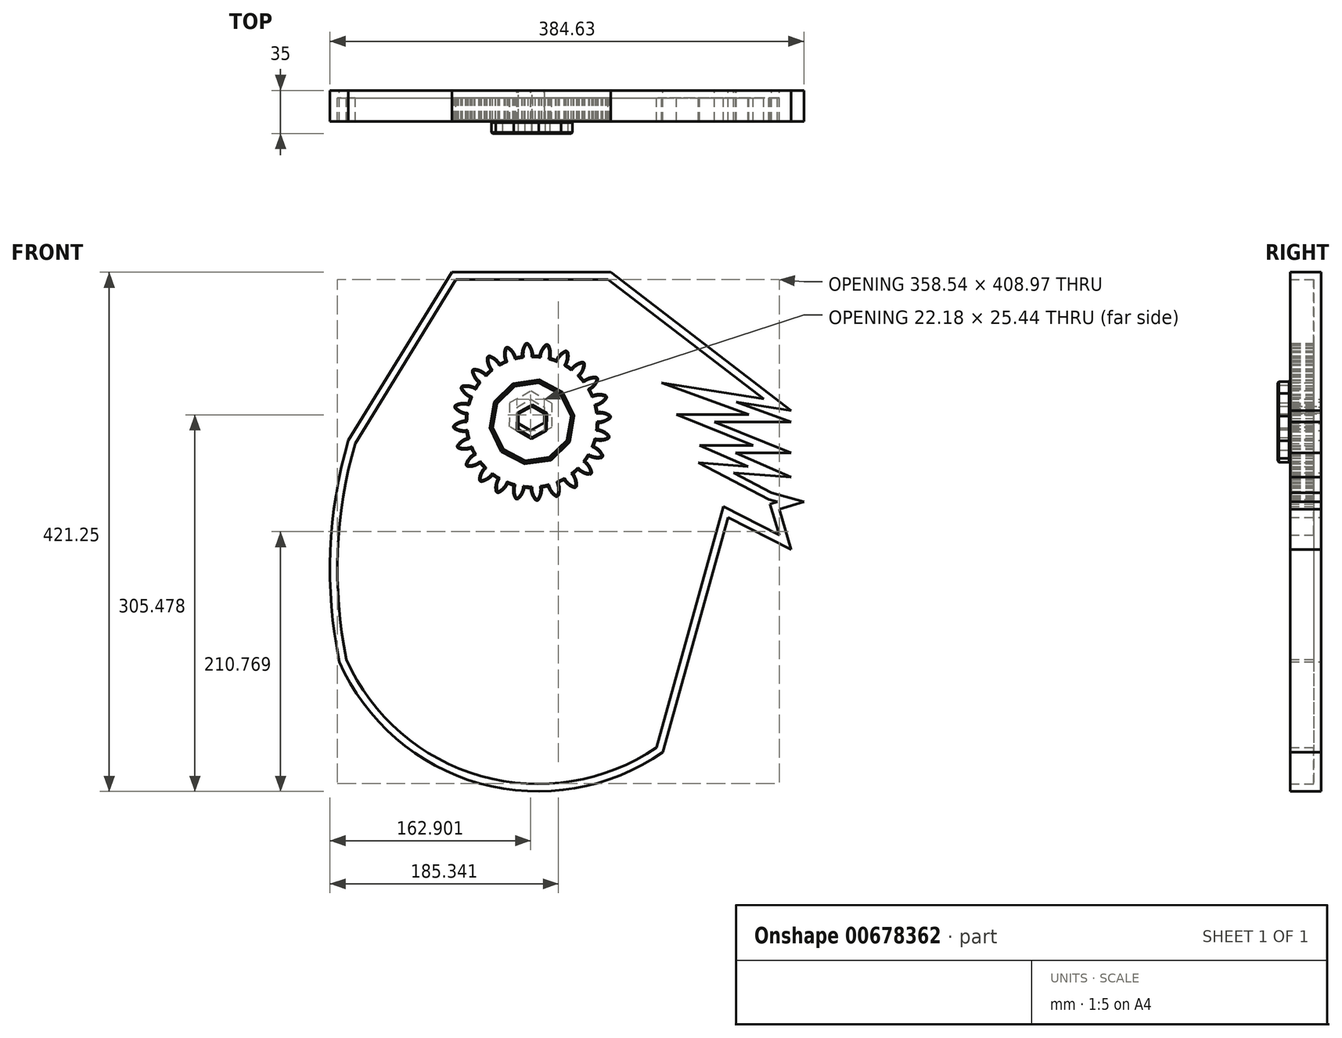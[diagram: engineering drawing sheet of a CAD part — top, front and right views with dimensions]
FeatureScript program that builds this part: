
annotation { "Feature Type Name" : "Feature", "Feature Type Description" : "" }
export const myFeature = defineFeature(function(context is Context, id is Id, definition is map)
    precondition{}
    {
        {
            var Q0;
            Q0=qCreatedBy(makeId("Front.planeOp"),FACE);
            var sketch = newSketch(context, id + "F0", { "sketchPlane" : qUnion([Q0])});
            skCircle(sketch, "E0", {"center": v(0, 0) * mm, "radius": 53.72 * mm});
            skCircle(sketch, "E1", {"center": v(0, 0) * mm, "radius": 58.67 * mm, "construction": true});
            skCircle(sketch, "E2", {"center": v(0, 0) * mm, "radius": 63.5 * mm, "construction": true});
            skLineSegment(sketch, "E3", {"start": v(0, 0) * mm, "end": v(0, 78.03) * mm, "construction": true});
            skLineSegment(sketch, "E4", {"start": v(0, 0) * mm, "end": v(-5.6, 85.42) * mm, "construction": true});
            skLineSegment(sketch, "E5", {"start": v(0, 58.67) * mm, "end": v(-59.1, 58.67) * mm, "construction": true});
            skLineSegment(sketch, "E6", {"start": v(0, 58.67) * mm, "end": v(-58.88, 37.24) * mm, "construction": true});
            skCircle(sketch, "E7", {"center": v(0, 0) * mm, "radius": 55.14 * mm, "construction": true});
            skCircle(sketch, "E8", {"center": v(0, 58.67) * mm, "radius": 14.6 * mm, "construction": true});
            skCircle(sketch, "E9", {"center": v(-13.72, 53.68) * mm, "radius": 14.6 * mm, "construction": true});
            skArc(sketch, "E10", {"start": v(0, 58.67) * mm, "mid": v(-1.2, 61.2) * mm, "end": v(-2.86, 63.44) * mm});
            skArc(sketch, "E11", {"start": v(0.88, 53.71) * mm, "mid": v(0.65, 56.23) * mm, "end": v(0, 58.67) * mm});
            skArc(sketch, "E12.MirrorCS", {"start": v(-7.66, 58.17) * mm, "mid": v(-6.8, 60.83) * mm, "end": v(-5.45, 63.27) * mm});
            skArc(sketch, "E13.MirrorCS", {"start": v(-7.88, 53.14) * mm, "mid": v(-7.99, 55.67) * mm, "end": v(-7.66, 58.17) * mm});
            skArc(sketch, "E14", {"start": v(-2.86, 63.44) * mm, "mid": v(-4.18, 63.85) * mm, "end": v(-5.45, 63.27) * mm});
            skCircle(sketch, "E15.cCircle", {"center": v(0, 0) * mm, "radius": 31.52 * mm, "construction": true});
            skLineSegment(sketch, "E15.0", {"start": v(-5.65, -32.65) * mm, "end": v(-23.76, -23.1) * mm});
            skLineSegment(sketch, "E15.1", {"start": v(-23.76, -23.1) * mm, "end": v(-32.8, -4.72) * mm});
            skLineSegment(sketch, "E15.2", {"start": v(-32.8, -4.72) * mm, "end": v(-29.31, 15.46) * mm});
            skLineSegment(sketch, "E15.3", {"start": v(-29.31, 15.46) * mm, "end": v(-14.63, 29.74) * mm});
            skLineSegment(sketch, "E15.4", {"start": v(-14.63, 29.74) * mm, "end": v(5.65, 32.65) * mm});
            skLineSegment(sketch, "E15.5", {"start": v(5.65, 32.65) * mm, "end": v(23.76, 23.1) * mm});
            skLineSegment(sketch, "E15.6", {"start": v(23.76, 23.1) * mm, "end": v(32.8, 4.72) * mm});
            skLineSegment(sketch, "E15.7", {"start": v(32.8, 4.72) * mm, "end": v(29.31, -15.46) * mm});
            skLineSegment(sketch, "E15.8", {"start": v(29.31, -15.46) * mm, "end": v(14.63, -29.74) * mm});
            skLineSegment(sketch, "E15.9", {"start": v(14.63, -29.74) * mm, "end": v(-5.65, -32.65) * mm});
            skPoint(sketch, "E15.0.midPoint", {"position": v(-14.7, -27.88) * mm});
            skCircle(sketch, "E16.cCircle", {"center": v(0, 0) * mm, "radius": 11.02 * mm, "construction": true});
            skLineSegment(sketch, "E16.0", {"start": v(-0.15, -12.72) * mm, "end": v(-11.1, -6.23) * mm});
            skLineSegment(sketch, "E16.1", {"start": v(-11.1, -6.23) * mm, "end": v(-10.94, 6.5) * mm});
            skLineSegment(sketch, "E16.2", {"start": v(-10.94, 6.5) * mm, "end": v(0.15, 12.72) * mm});
            skLineSegment(sketch, "E16.3", {"start": v(0.15, 12.72) * mm, "end": v(11.1, 6.23) * mm});
            skLineSegment(sketch, "E16.4", {"start": v(11.1, 6.23) * mm, "end": v(10.94, -6.5) * mm});
            skLineSegment(sketch, "E16.5", {"start": v(10.94, -6.5) * mm, "end": v(-0.15, -12.72) * mm});
            skPoint(sketch, "E16.0.midPoint", {"position": v(-5.62, -9.48) * mm});
            skSolve(sketch);
        }
        {
            var Q0;
            {var subQ0=sQuery(id+"F0.wireOp",EDGE,"E0");var subQ1=makeQuery(id+"F0.imprint","INTERSECT",VERTEX,{"derivedFrom":[subQ0,sQuery(id+"F0.wireOp",EDGE,"E11")]});Q0=makeQuery(id+"F0.imprint","IMPRINT",FACE,{"disambiguationData":[TD([[makeQuery(id+"F0.imprint","IMPRINT",EDGE,{"disambiguationData":[TD([[subQ1,-1.0]])],"derivedFrom":subQ0}),1.0]])]});}
            var Q1;
            Q1=makeQuery(id+"F0.imprint","IMPRINT",FACE,{"disambiguationData":[TD([[makeQuery(id+"F0.imprint","IMPRINT",EDGE,{"derivedFrom":sQuery(id+"F0.wireOp",EDGE,"E10")}),1.0]])]});
            extrude(context, id + "F1", {"entities" : qUnion([Q0, Q1]), "depth" : 25 * mm, "offsetDistance" : 25 * mm});
        }
        {
            var Q0;
            Q0=makeQuery(id+"F1.opExtrude","SWEPT_BODY",BODY,{"disambiguationData":[OSD([sQuery(id+"F0.wireOp",EDGE,"E0"),sQuery(id+"F0.wireOp",EDGE,"E10"),sQuery(id+"F0.wireOp",EDGE,"E11"),sQuery(id+"F0.wireOp",EDGE,"E12.MirrorCS"),sQuery(id+"F0.wireOp",EDGE,"E13.MirrorCS"),sQuery(id+"F0.wireOp",EDGE,"E14")])]});
            var Q1;
            Q1=makeQuery(id+"F1.opExtrude","SWEPT_FACE",FACE,{"disambiguationData":[OSD([sQuery(id+"F0.wireOp",EDGE,"E0")])]});
            circularPattern(context, id + "F2", {"entities" : qUnion([Q0]), "axis" : qUnion([Q1]), "angle" : 360 * degree, "instanceCount" : 24, "equalSpace" : true});
        }
        {
            var Q0;
            Q0=makeQuery(id+"F0.imprint","IMPRINT",FACE,{"disambiguationData":[TD([[makeQuery(id+"F0.imprint","IMPRINT",EDGE,{"derivedFrom":sQuery(id+"F0.wireOp",EDGE,"E15.0")}),-1.0]])]});
            extrude(context, id + "F3", {"entities" : qUnion([Q0]), "operationType" : NewBodyOperationType.ADD, "depth" : 35 * mm, "offsetDistance" : 25 * mm});
        }
        {
            var Q0;
            {var subQ0=makeQuery(id+"F1.opExtrude","CAP_FACE",FACE,{"disambiguationData":[OSD([sQuery(id+"F0.wireOp",EDGE,"E0"),sQuery(id+"F0.wireOp",EDGE,"E10"),sQuery(id+"F0.wireOp",EDGE,"E11"),sQuery(id+"F0.wireOp",EDGE,"E12.MirrorCS"),sQuery(id+"F0.wireOp",EDGE,"E13.MirrorCS"),sQuery(id+"F0.wireOp",EDGE,"E14"),sQuery(id+"F0.wireOp",EDGE,"E15.0"),sQuery(id+"F0.wireOp",EDGE,"E15.1"),sQuery(id+"F0.wireOp",EDGE,"E15.2"),sQuery(id+"F0.wireOp",EDGE,"E15.3"),sQuery(id+"F0.wireOp",EDGE,"E15.4"),sQuery(id+"F0.wireOp",EDGE,"E15.5"),sQuery(id+"F0.wireOp",EDGE,"E15.6"),sQuery(id+"F0.wireOp",EDGE,"E15.7"),sQuery(id+"F0.wireOp",EDGE,"E15.8"),sQuery(id+"F0.wireOp",EDGE,"E15.9")])],"isStart":false});Q0=makeQuery(id+"F3.boolean.opBoolean","MERGE",FACE,{"derivedFrom":[subQ0,makeQuery(id+"F2.opPattern","COPY",FACE,{"derivedFrom":subQ0,"instanceName":"1"}),makeQuery(id+"F2.opPattern","COPY",FACE,{"derivedFrom":subQ0,"instanceName":"2"}),makeQuery(id+"F2.opPattern","COPY",FACE,{"derivedFrom":subQ0,"instanceName":"3"}),makeQuery(id+"F2.opPattern","COPY",FACE,{"derivedFrom":subQ0,"instanceName":"4"}),makeQuery(id+"F2.opPattern","COPY",FACE,{"derivedFrom":subQ0,"instanceName":"5"}),makeQuery(id+"F2.opPattern","COPY",FACE,{"derivedFrom":subQ0,"instanceName":"6"}),makeQuery(id+"F2.opPattern","COPY",FACE,{"derivedFrom":subQ0,"instanceName":"7"}),makeQuery(id+"F2.opPattern","COPY",FACE,{"derivedFrom":subQ0,"instanceName":"8"}),makeQuery(id+"F2.opPattern","COPY",FACE,{"derivedFrom":subQ0,"instanceName":"9"}),makeQuery(id+"F2.opPattern","COPY",FACE,{"derivedFrom":subQ0,"instanceName":"10"}),makeQuery(id+"F2.opPattern","COPY",FACE,{"derivedFrom":subQ0,"instanceName":"11"}),makeQuery(id+"F2.opPattern","COPY",FACE,{"derivedFrom":subQ0,"instanceName":"12"}),makeQuery(id+"F2.opPattern","COPY",FACE,{"derivedFrom":subQ0,"instanceName":"13"}),makeQuery(id+"F2.opPattern","COPY",FACE,{"derivedFrom":subQ0,"instanceName":"14"}),makeQuery(id+"F2.opPattern","COPY",FACE,{"derivedFrom":subQ0,"instanceName":"15"}),makeQuery(id+"F2.opPattern","COPY",FACE,{"derivedFrom":subQ0,"instanceName":"16"}),makeQuery(id+"F2.opPattern","COPY",FACE,{"derivedFrom":subQ0,"instanceName":"17"}),makeQuery(id+"F2.opPattern","COPY",FACE,{"derivedFrom":subQ0,"instanceName":"18"}),makeQuery(id+"F2.opPattern","COPY",FACE,{"derivedFrom":subQ0,"instanceName":"19"}),makeQuery(id+"F2.opPattern","COPY",FACE,{"derivedFrom":subQ0,"instanceName":"20"}),makeQuery(id+"F2.opPattern","COPY",FACE,{"derivedFrom":subQ0,"instanceName":"21"}),makeQuery(id+"F2.opPattern","COPY",FACE,{"derivedFrom":subQ0,"instanceName":"22"}),makeQuery(id+"F2.opPattern","COPY",FACE,{"derivedFrom":subQ0,"instanceName":"23"})]});}
            var Q1;
            Q1=makeQuery(id+"F3.opExtrude","CAP_FACE",FACE,{"disambiguationData":[OSD([sQuery(id+"F0.wireOp",EDGE,"E15.0"),sQuery(id+"F0.wireOp",EDGE,"E15.1"),sQuery(id+"F0.wireOp",EDGE,"E15.2"),sQuery(id+"F0.wireOp",EDGE,"E15.3"),sQuery(id+"F0.wireOp",EDGE,"E15.4"),sQuery(id+"F0.wireOp",EDGE,"E15.5"),sQuery(id+"F0.wireOp",EDGE,"E15.6"),sQuery(id+"F0.wireOp",EDGE,"E15.7"),sQuery(id+"F0.wireOp",EDGE,"E15.8"),sQuery(id+"F0.wireOp",EDGE,"E15.9"),sQuery(id+"F0.wireOp",EDGE,"E16.0"),sQuery(id+"F0.wireOp",EDGE,"E16.1"),sQuery(id+"F0.wireOp",EDGE,"E16.2"),sQuery(id+"F0.wireOp",EDGE,"E16.3"),sQuery(id+"F0.wireOp",EDGE,"E16.4"),sQuery(id+"F0.wireOp",EDGE,"E16.5")])],"isStart":false});
            chamfer(context, id + "F4", {"entities" : qUnion([Q0, Q1]), "width" : 1 * mm, "tangentPropagation" : true});
        }
        {
            var Q0;
            Q0=qCreatedBy(makeId("Front.planeOp"),FACE);
            var sketch = newSketch(context, id + "F5", { "sketchPlane" : qUnion([Q0])});
            skLineSegment(sketch, "E17", {"start": v(-148.99, -15.01) * mm, "end": v(-65.1, 121.38) * mm});
            skLineSegment(sketch, "E18", {"start": v(-65.1, 121.38) * mm, "end": v(63.89, 121.38) * mm});
            skLineSegment(sketch, "E19", {"start": v(63.89, 121.38) * mm, "end": v(210.45, 9.15) * mm});
            skArc(sketch, "E20", {"start": v(-148.99, -15.01) * mm, "mid": v(-163.6, -104.42) * mm, "end": v(-156.33, -194.72) * mm});
            skArc(sketch, "E21", {"start": v(-156.33, -194.72) * mm, "mid": v(-42.34, -293.39) * mm, "end": v(106.25, -267.95) * mm});
            skLineSegment(sketch, "E22", {"start": v(210.45, 9.15) * mm, "end": v(165.85, 16.1) * mm});
            skLineSegment(sketch, "E23", {"start": v(165.85, 16.1) * mm, "end": v(210.45, 0) * mm});
            skLineSegment(sketch, "E24", {"start": v(148.15, 0) * mm, "end": v(210.45, 0) * mm});
            skLineSegment(sketch, "E25", {"start": v(148.15, 0) * mm, "end": v(210.45, -25.18) * mm});
            skLineSegment(sketch, "E26", {"start": v(165.1, -25.18) * mm, "end": v(210.45, -25.18) * mm});
            skLineSegment(sketch, "E27", {"start": v(210.45, -44.82) * mm, "end": v(165.1, -25.18) * mm});
            skLineSegment(sketch, "E28", {"start": v(163.6, -41.3) * mm, "end": v(210.45, -44.82) * mm});
            skLineSegment(sketch, "E29", {"start": v(163.6, -41.3) * mm, "end": v(194.33, -57.47) * mm});
            skLineSegment(sketch, "E30", {"start": v(220.71, -64.83) * mm, "end": v(194.33, -57.47) * mm});
            skLineSegment(sketch, "E31", {"start": v(220.71, -64.83) * mm, "end": v(200.67, -70.81) * mm});
            skLineSegment(sketch, "E32", {"start": v(200.67, -70.81) * mm, "end": v(210.45, -103.6) * mm});
            skLineSegment(sketch, "E33", {"start": v(210.45, -103.6) * mm, "end": v(210.45, -103.6) * mm});
            skLineSegment(sketch, "E34", {"start": v(210.45, -103.6) * mm, "end": v(159.32, -77.52) * mm});
            skLineSegment(sketch, "E35", {"start": v(159.32, -77.52) * mm, "end": v(106.25, -267.95) * mm});
            skCircle(sketch, "E36.cCircle", {"center": v(-1.02, 5.6) * mm, "radius": 11.02 * mm, "construction": true});
            skLineSegment(sketch, "E36.0", {"start": v(-1.17, -7.11) * mm, "end": v(-12.11, -0.62) * mm});
            skLineSegment(sketch, "E36.1", {"start": v(-12.11, -0.62) * mm, "end": v(-11.96, 12.1) * mm});
            skLineSegment(sketch, "E36.2", {"start": v(-11.96, 12.1) * mm, "end": v(-0.87, 18.33) * mm});
            skLineSegment(sketch, "E36.3", {"start": v(-0.87, 18.33) * mm, "end": v(10.07, 11.84) * mm});
            skLineSegment(sketch, "E36.4", {"start": v(10.07, 11.84) * mm, "end": v(9.92, -0.88) * mm});
            skLineSegment(sketch, "E36.5", {"start": v(9.92, -0.88) * mm, "end": v(-1.17, -7.11) * mm});
            skSolve(sketch);
        }
        {
            var Q0;
            Q0=makeQuery(id+"F5.imprint","IMPRINT",FACE,{"disambiguationData":[TD([[makeQuery(id+"F5.imprint","IMPRINT",EDGE,{"derivedFrom":sQuery(id+"F5.wireOp",EDGE,"E17")}),-1.0]])]});
            extrude(context, id + "F6", {"entities" : qUnion([Q0]), "depth" : 25 * mm, "offsetDistance" : 25 * mm});
        }
        {
            var Q0;
            Q0=makeQuery(id+"F6.opExtrude","CAP_FACE",FACE,{"disambiguationData":[OSD([sQuery(id+"F5.wireOp",EDGE,"E17"),sQuery(id+"F5.wireOp",EDGE,"E18"),sQuery(id+"F5.wireOp",EDGE,"E19"),sQuery(id+"F5.wireOp",EDGE,"E20"),sQuery(id+"F5.wireOp",EDGE,"E21"),sQuery(id+"F5.wireOp",EDGE,"E22"),sQuery(id+"F5.wireOp",EDGE,"E23"),sQuery(id+"F5.wireOp",EDGE,"E24"),sQuery(id+"F5.wireOp",EDGE,"E25"),sQuery(id+"F5.wireOp",EDGE,"E26"),sQuery(id+"F5.wireOp",EDGE,"E27"),sQuery(id+"F5.wireOp",EDGE,"E28"),sQuery(id+"F5.wireOp",EDGE,"E29"),sQuery(id+"F5.wireOp",EDGE,"E30"),sQuery(id+"F5.wireOp",EDGE,"E31"),sQuery(id+"F5.wireOp",EDGE,"E32"),sQuery(id+"F5.wireOp",EDGE,"E33"),sQuery(id+"F5.wireOp",EDGE,"E34"),sQuery(id+"F5.wireOp",EDGE,"E35")])],"isStart":false});
            shell(context, id + "F7", {"entities" : qUnion([Q0]), "thickness" : 6 * mm});
        }
    });
